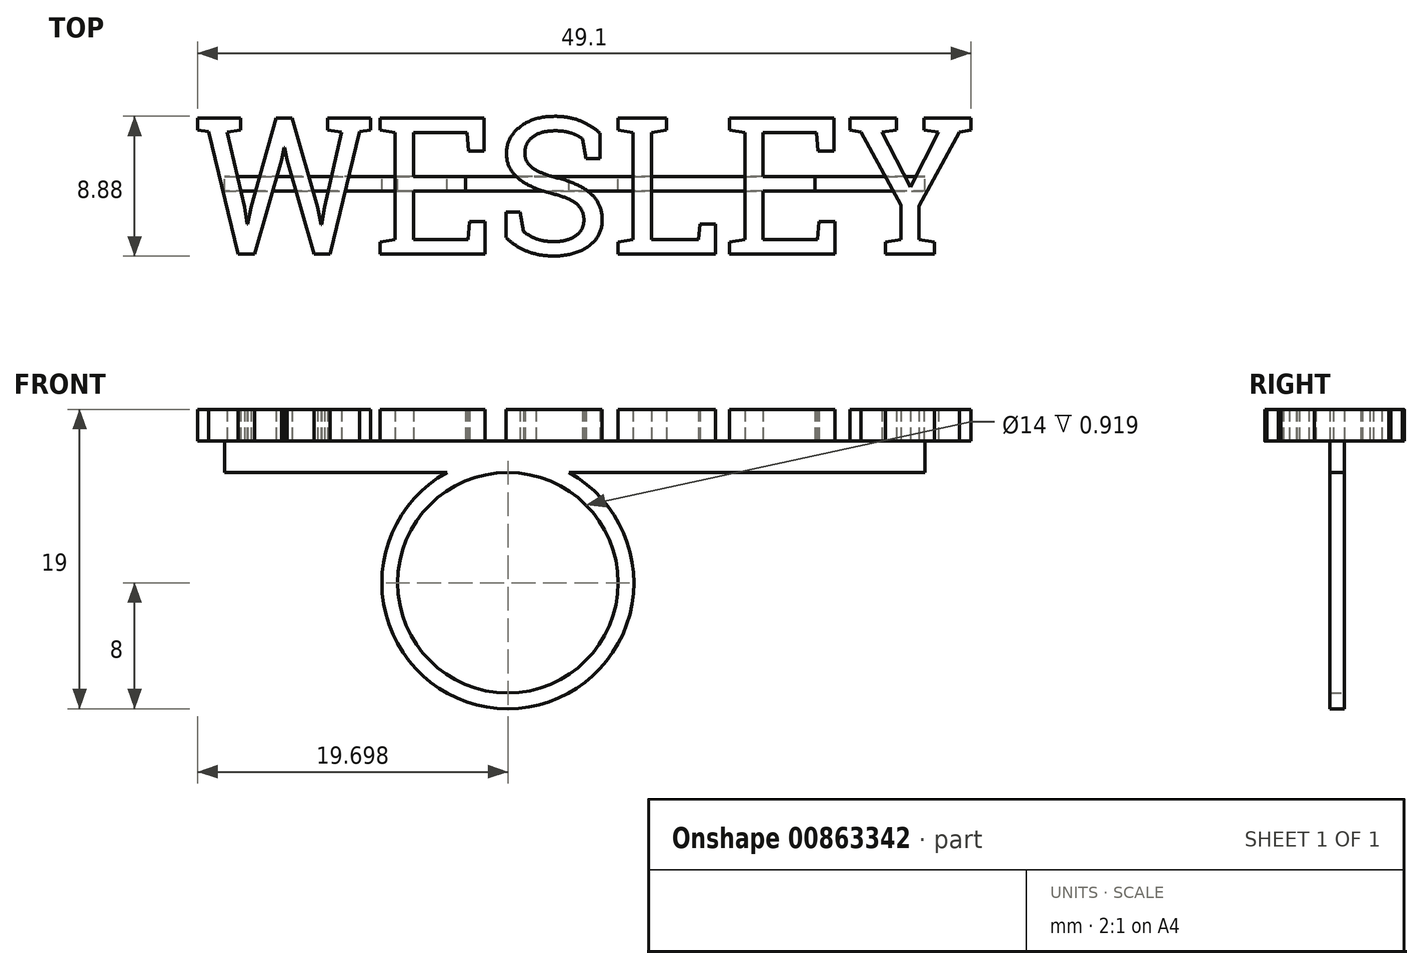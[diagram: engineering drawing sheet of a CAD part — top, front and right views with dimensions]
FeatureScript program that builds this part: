
annotation { "Feature Type Name" : "Feature", "Feature Type Description" : "" }
export const myFeature = defineFeature(function(context is Context, id is Id, definition is map)
    precondition{}
    {
        {
            var Q0;
            Q0=qCreatedBy(makeId("Top.planeOp"),FACE);
            var sketch = newSketch(context, id + "F0", { "sketchPlane" : qUnion([Q0])});
            skText(sketch, "E0", { "text": "WESLEY", "fontName": "RobotoSlab-Regular.ttf"});
            const initialGuessF0  = {"E0": [0, 0, 1, 0, 0.00873]};
            skSetInitialGuess(sketch, initialGuessF0);
            skSolve(sketch);
        }
        {
            var Q0;
            Q0=qSketchRegion(id+"F0",true);
            extrude(context, id + "F1", {"entities" : qUnion([Q0]), "depth" : 2 * mm, "offsetDistance" : 25 * mm});
        }
        {
            var Q0;
            Q0=makeQuery(id+"F1.opExtrude","CAP_FACE",FACE,{"disambiguationData":[OSD([sQuery(id+"F0.wireOp",EDGE,"E0.sketch_text.stroke-30"),sQuery(id+"F0.wireOp",EDGE,"E0.sketch_text.stroke-31"),sQuery(id+"F0.wireOp",EDGE,"E0.sketch_text.stroke-32"),sQuery(id+"F0.wireOp",EDGE,"E0.sketch_text.stroke-33"),sQuery(id+"F0.wireOp",EDGE,"E0.sketch_text.stroke-34"),sQuery(id+"F0.wireOp",EDGE,"E0.sketch_text.stroke-35"),sQuery(id+"F0.wireOp",EDGE,"E0.sketch_text.stroke-36"),sQuery(id+"F0.wireOp",EDGE,"E0.sketch_text.stroke-37"),sQuery(id+"F0.wireOp",EDGE,"E0.sketch_text.stroke-38"),sQuery(id+"F0.wireOp",EDGE,"E0.sketch_text.stroke-39"),sQuery(id+"F0.wireOp",EDGE,"E0.sketch_text.stroke-40"),sQuery(id+"F0.wireOp",EDGE,"E0.sketch_text.stroke-41"),sQuery(id+"F0.wireOp",EDGE,"E0.sketch_text.stroke-42"),sQuery(id+"F0.wireOp",EDGE,"E0.sketch_text.stroke-43"),sQuery(id+"F0.wireOp",EDGE,"E0.sketch_text.stroke-44"),sQuery(id+"F0.wireOp",EDGE,"E0.sketch_text.stroke-45"),sQuery(id+"F0.wireOp",EDGE,"E0.sketch_text.stroke-46"),sQuery(id+"F0.wireOp",EDGE,"E0.sketch_text.stroke-47"),sQuery(id+"F0.wireOp",EDGE,"E0.sketch_text.stroke-48"),sQuery(id+"F0.wireOp",EDGE,"E0.sketch_text.stroke-49")])],"isStart":true});
            var sketch = newSketch(context, id + "F2", { "sketchPlane" : qUnion([Q0])});
            skLineSegment(sketch, "E1.bottom", {"start": v(13.86, -4) * mm, "end": v(46.36, -4) * mm});
            skLineSegment(sketch, "E1.top", {"start": v(13.86, -4.91) * mm, "end": v(46.36, -4.91) * mm});
            skLineSegment(sketch, "E1.left", {"start": v(13.86, -4) * mm, "end": v(13.86, -4.91) * mm});
            skLineSegment(sketch, "E1.right", {"start": v(46.36, -4) * mm, "end": v(46.36, -4.91) * mm});
            skLineSegment(sketch, "E2.bottom", {"start": v(13.86, -4) * mm, "end": v(1.86, -4) * mm});
            skLineSegment(sketch, "E2.top", {"start": v(13.86, -4.91) * mm, "end": v(1.86, -4.91) * mm});
            skLineSegment(sketch, "E2.right", {"start": v(1.86, -4) * mm, "end": v(1.86, -4.91) * mm});
            skSolve(sketch);
        }
        {
            var Q0;
            Q0=qSketchRegion(id+"F2",true);
            extrude(context, id + "F3", {"entities" : qUnion([Q0]), "depth" : 2 * mm, "offsetDistance" : 25 * mm});
        }
        {
            var Q0;
            Q0=makeQuery(id+"F1.opExtrude","SWEPT_BODY",BODY,{"disambiguationData":[OSD([sQuery(id+"F0.wireOp",EDGE,"E0.sketch_text.stroke-0"),sQuery(id+"F0.wireOp",EDGE,"E0.sketch_text.stroke-1"),sQuery(id+"F0.wireOp",EDGE,"E0.sketch_text.stroke-2"),sQuery(id+"F0.wireOp",EDGE,"E0.sketch_text.stroke-3"),sQuery(id+"F0.wireOp",EDGE,"E0.sketch_text.stroke-4"),sQuery(id+"F0.wireOp",EDGE,"E0.sketch_text.stroke-5"),sQuery(id+"F0.wireOp",EDGE,"E0.sketch_text.stroke-6"),sQuery(id+"F0.wireOp",EDGE,"E0.sketch_text.stroke-7"),sQuery(id+"F0.wireOp",EDGE,"E0.sketch_text.stroke-8"),sQuery(id+"F0.wireOp",EDGE,"E0.sketch_text.stroke-9"),sQuery(id+"F0.wireOp",EDGE,"E0.sketch_text.stroke-10"),sQuery(id+"F0.wireOp",EDGE,"E0.sketch_text.stroke-11"),sQuery(id+"F0.wireOp",EDGE,"E0.sketch_text.stroke-12"),sQuery(id+"F0.wireOp",EDGE,"E0.sketch_text.stroke-13"),sQuery(id+"F0.wireOp",EDGE,"E0.sketch_text.stroke-14"),sQuery(id+"F0.wireOp",EDGE,"E0.sketch_text.stroke-15"),sQuery(id+"F0.wireOp",EDGE,"E0.sketch_text.stroke-16"),sQuery(id+"F0.wireOp",EDGE,"E0.sketch_text.stroke-17"),sQuery(id+"F0.wireOp",EDGE,"E0.sketch_text.stroke-18"),sQuery(id+"F0.wireOp",EDGE,"E0.sketch_text.stroke-19"),sQuery(id+"F0.wireOp",EDGE,"E0.sketch_text.stroke-20"),sQuery(id+"F0.wireOp",EDGE,"E0.sketch_text.stroke-21"),sQuery(id+"F0.wireOp",EDGE,"E0.sketch_text.stroke-22"),sQuery(id+"F0.wireOp",EDGE,"E0.sketch_text.stroke-23"),sQuery(id+"F0.wireOp",EDGE,"E0.sketch_text.stroke-24"),sQuery(id+"F0.wireOp",EDGE,"E0.sketch_text.stroke-25"),sQuery(id+"F0.wireOp",EDGE,"E0.sketch_text.stroke-26"),sQuery(id+"F0.wireOp",EDGE,"E0.sketch_text.stroke-27"),sQuery(id+"F0.wireOp",EDGE,"E0.sketch_text.stroke-28"),sQuery(id+"F0.wireOp",EDGE,"E0.sketch_text.stroke-29")])]});
            var Q1;
            Q1=makeQuery(id+"F3.opExtrude","SWEPT_BODY",BODY,{"disambiguationData":[OSD([sQuery(id+"F2.wireOp",EDGE,"E1.bottom"),sQuery(id+"F2.wireOp",EDGE,"E1.top"),sQuery(id+"F2.wireOp",EDGE,"E1.right"),sQuery(id+"F2.wireOp",EDGE,"E2.bottom"),sQuery(id+"F2.wireOp",EDGE,"E2.top"),sQuery(id+"F2.wireOp",EDGE,"E2.right")])]});
            var Q2;
            Q2=makeQuery(id+"F1.opExtrude","SWEPT_BODY",BODY,{"disambiguationData":[OSD([sQuery(id+"F0.wireOp",EDGE,"E0.sketch_text.stroke-30"),sQuery(id+"F0.wireOp",EDGE,"E0.sketch_text.stroke-31"),sQuery(id+"F0.wireOp",EDGE,"E0.sketch_text.stroke-32"),sQuery(id+"F0.wireOp",EDGE,"E0.sketch_text.stroke-33"),sQuery(id+"F0.wireOp",EDGE,"E0.sketch_text.stroke-34"),sQuery(id+"F0.wireOp",EDGE,"E0.sketch_text.stroke-35"),sQuery(id+"F0.wireOp",EDGE,"E0.sketch_text.stroke-36"),sQuery(id+"F0.wireOp",EDGE,"E0.sketch_text.stroke-37"),sQuery(id+"F0.wireOp",EDGE,"E0.sketch_text.stroke-38"),sQuery(id+"F0.wireOp",EDGE,"E0.sketch_text.stroke-39"),sQuery(id+"F0.wireOp",EDGE,"E0.sketch_text.stroke-40"),sQuery(id+"F0.wireOp",EDGE,"E0.sketch_text.stroke-41"),sQuery(id+"F0.wireOp",EDGE,"E0.sketch_text.stroke-42"),sQuery(id+"F0.wireOp",EDGE,"E0.sketch_text.stroke-43"),sQuery(id+"F0.wireOp",EDGE,"E0.sketch_text.stroke-44"),sQuery(id+"F0.wireOp",EDGE,"E0.sketch_text.stroke-45"),sQuery(id+"F0.wireOp",EDGE,"E0.sketch_text.stroke-46"),sQuery(id+"F0.wireOp",EDGE,"E0.sketch_text.stroke-47"),sQuery(id+"F0.wireOp",EDGE,"E0.sketch_text.stroke-48"),sQuery(id+"F0.wireOp",EDGE,"E0.sketch_text.stroke-49")])]});
            var Q3;
            Q3=makeQuery(id+"F1.opExtrude","SWEPT_BODY",BODY,{"disambiguationData":[OSD([sQuery(id+"F0.wireOp",EDGE,"E0.sketch_text.stroke-50"),sQuery(id+"F0.wireOp",EDGE,"E0.sketch_text.stroke-51"),sQuery(id+"F0.wireOp",EDGE,"E0.sketch_text.stroke-52"),sQuery(id+"F0.wireOp",EDGE,"E0.sketch_text.stroke-53"),sQuery(id+"F0.wireOp",EDGE,"E0.sketch_text.stroke-54"),sQuery(id+"F0.wireOp",EDGE,"E0.sketch_text.stroke-55"),sQuery(id+"F0.wireOp",EDGE,"E0.sketch_text.stroke-56"),sQuery(id+"F0.wireOp",EDGE,"E0.sketch_text.stroke-57"),sQuery(id+"F0.wireOp",EDGE,"E0.sketch_text.stroke-58"),sQuery(id+"F0.wireOp",EDGE,"E0.sketch_text.stroke-59"),sQuery(id+"F0.wireOp",EDGE,"E0.sketch_text.stroke-60"),sQuery(id+"F0.wireOp",EDGE,"E0.sketch_text.stroke-61"),sQuery(id+"F0.wireOp",EDGE,"E0.sketch_text.stroke-62"),sQuery(id+"F0.wireOp",EDGE,"E0.sketch_text.stroke-63"),sQuery(id+"F0.wireOp",EDGE,"E0.sketch_text.stroke-64"),sQuery(id+"F0.wireOp",EDGE,"E0.sketch_text.stroke-65"),sQuery(id+"F0.wireOp",EDGE,"E0.sketch_text.stroke-66"),sQuery(id+"F0.wireOp",EDGE,"E0.sketch_text.stroke-67"),sQuery(id+"F0.wireOp",EDGE,"E0.sketch_text.stroke-68"),sQuery(id+"F0.wireOp",EDGE,"E0.sketch_text.stroke-69"),sQuery(id+"F0.wireOp",EDGE,"E0.sketch_text.stroke-70"),sQuery(id+"F0.wireOp",EDGE,"E0.sketch_text.stroke-71"),sQuery(id+"F0.wireOp",EDGE,"E0.sketch_text.stroke-72"),sQuery(id+"F0.wireOp",EDGE,"E0.sketch_text.stroke-73"),sQuery(id+"F0.wireOp",EDGE,"E0.sketch_text.stroke-74"),sQuery(id+"F0.wireOp",EDGE,"E0.sketch_text.stroke-75"),sQuery(id+"F0.wireOp",EDGE,"E0.sketch_text.stroke-76"),sQuery(id+"F0.wireOp",EDGE,"E0.sketch_text.stroke-77"),sQuery(id+"F0.wireOp",EDGE,"E0.sketch_text.stroke-78"),sQuery(id+"F0.wireOp",EDGE,"E0.sketch_text.stroke-79")])]});
            var Q4;
            Q4=makeQuery(id+"F1.opExtrude","SWEPT_BODY",BODY,{"disambiguationData":[OSD([sQuery(id+"F0.wireOp",EDGE,"E0.sketch_text.stroke-80"),sQuery(id+"F0.wireOp",EDGE,"E0.sketch_text.stroke-81"),sQuery(id+"F0.wireOp",EDGE,"E0.sketch_text.stroke-82"),sQuery(id+"F0.wireOp",EDGE,"E0.sketch_text.stroke-83"),sQuery(id+"F0.wireOp",EDGE,"E0.sketch_text.stroke-84"),sQuery(id+"F0.wireOp",EDGE,"E0.sketch_text.stroke-85"),sQuery(id+"F0.wireOp",EDGE,"E0.sketch_text.stroke-86"),sQuery(id+"F0.wireOp",EDGE,"E0.sketch_text.stroke-87"),sQuery(id+"F0.wireOp",EDGE,"E0.sketch_text.stroke-88"),sQuery(id+"F0.wireOp",EDGE,"E0.sketch_text.stroke-89"),sQuery(id+"F0.wireOp",EDGE,"E0.sketch_text.stroke-90"),sQuery(id+"F0.wireOp",EDGE,"E0.sketch_text.stroke-91"),sQuery(id+"F0.wireOp",EDGE,"E0.sketch_text.stroke-92"),sQuery(id+"F0.wireOp",EDGE,"E0.sketch_text.stroke-93"),sQuery(id+"F0.wireOp",EDGE,"E0.sketch_text.stroke-94"),sQuery(id+"F0.wireOp",EDGE,"E0.sketch_text.stroke-95")])]});
            var Q5;
            Q5=makeQuery(id+"F1.opExtrude","SWEPT_BODY",BODY,{"disambiguationData":[OSD([sQuery(id+"F0.wireOp",EDGE,"E0.sketch_text.stroke-96"),sQuery(id+"F0.wireOp",EDGE,"E0.sketch_text.stroke-97"),sQuery(id+"F0.wireOp",EDGE,"E0.sketch_text.stroke-98"),sQuery(id+"F0.wireOp",EDGE,"E0.sketch_text.stroke-99"),sQuery(id+"F0.wireOp",EDGE,"E0.sketch_text.stroke-100"),sQuery(id+"F0.wireOp",EDGE,"E0.sketch_text.stroke-101"),sQuery(id+"F0.wireOp",EDGE,"E0.sketch_text.stroke-102"),sQuery(id+"F0.wireOp",EDGE,"E0.sketch_text.stroke-103"),sQuery(id+"F0.wireOp",EDGE,"E0.sketch_text.stroke-104"),sQuery(id+"F0.wireOp",EDGE,"E0.sketch_text.stroke-105"),sQuery(id+"F0.wireOp",EDGE,"E0.sketch_text.stroke-106"),sQuery(id+"F0.wireOp",EDGE,"E0.sketch_text.stroke-107"),sQuery(id+"F0.wireOp",EDGE,"E0.sketch_text.stroke-108"),sQuery(id+"F0.wireOp",EDGE,"E0.sketch_text.stroke-109"),sQuery(id+"F0.wireOp",EDGE,"E0.sketch_text.stroke-110"),sQuery(id+"F0.wireOp",EDGE,"E0.sketch_text.stroke-111"),sQuery(id+"F0.wireOp",EDGE,"E0.sketch_text.stroke-112"),sQuery(id+"F0.wireOp",EDGE,"E0.sketch_text.stroke-113"),sQuery(id+"F0.wireOp",EDGE,"E0.sketch_text.stroke-114"),sQuery(id+"F0.wireOp",EDGE,"E0.sketch_text.stroke-115")])]});
            var Q6;
            Q6=makeQuery(id+"F1.opExtrude","SWEPT_BODY",BODY,{"disambiguationData":[OSD([sQuery(id+"F0.wireOp",EDGE,"E0.sketch_text.stroke-116"),sQuery(id+"F0.wireOp",EDGE,"E0.sketch_text.stroke-117"),sQuery(id+"F0.wireOp",EDGE,"E0.sketch_text.stroke-118"),sQuery(id+"F0.wireOp",EDGE,"E0.sketch_text.stroke-119"),sQuery(id+"F0.wireOp",EDGE,"E0.sketch_text.stroke-120"),sQuery(id+"F0.wireOp",EDGE,"E0.sketch_text.stroke-121"),sQuery(id+"F0.wireOp",EDGE,"E0.sketch_text.stroke-122"),sQuery(id+"F0.wireOp",EDGE,"E0.sketch_text.stroke-123"),sQuery(id+"F0.wireOp",EDGE,"E0.sketch_text.stroke-124"),sQuery(id+"F0.wireOp",EDGE,"E0.sketch_text.stroke-125"),sQuery(id+"F0.wireOp",EDGE,"E0.sketch_text.stroke-126"),sQuery(id+"F0.wireOp",EDGE,"E0.sketch_text.stroke-127"),sQuery(id+"F0.wireOp",EDGE,"E0.sketch_text.stroke-128"),sQuery(id+"F0.wireOp",EDGE,"E0.sketch_text.stroke-129"),sQuery(id+"F0.wireOp",EDGE,"E0.sketch_text.stroke-130"),sQuery(id+"F0.wireOp",EDGE,"E0.sketch_text.stroke-131"),sQuery(id+"F0.wireOp",EDGE,"E0.sketch_text.stroke-132"),sQuery(id+"F0.wireOp",EDGE,"E0.sketch_text.stroke-133"),sQuery(id+"F0.wireOp",EDGE,"E0.sketch_text.stroke-134"),sQuery(id+"F0.wireOp",EDGE,"E0.sketch_text.stroke-135"),sQuery(id+"F0.wireOp",EDGE,"E0.sketch_text.stroke-136")])]});
            booleanBodies(context, id + "F4", {"operationType" : BooleanOperationType.UNION, "tools" : qUnion([Q0, Q1, Q2, Q3, Q4, Q5, Q6])});
        }
        {
            var Q0;
            Q0=makeQuery(id+"F4.opBoolean","MERGE",FACE,{"derivedFrom":[makeQuery(id+"F1.opExtrude","SWEPT_FACE",FACE,{"disambiguationData":[OSD([sQuery(id+"F0.wireOp",EDGE,"E0.sketch_text.stroke-41")])]}),makeQuery(id+"F1.opExtrude","SWEPT_FACE",FACE,{"disambiguationData":[OSD([sQuery(id+"F0.wireOp",EDGE,"E0.sketch_text.stroke-107")])]}),makeQuery(id+"F3.opExtrude","SWEPT_FACE",FACE,{"disambiguationData":[OSD([sQuery(id+"F2.wireOp",EDGE,"E1.top"),sQuery(id+"F2.wireOp",EDGE,"E2.top")])]})]});
            var sketch = newSketch(context, id + "F5", { "sketchPlane" : qUnion([Q0])});
            skCircle(sketch, "E3", {"center": v(-19.86, -9) * mm, "radius": 7 * mm});
            skLineSegment(sketch, "E4", {"start": v(-1.86, -2) * mm, "end": v(-19.86, -2) * mm, "construction": true});
            skCircle(sketch, "E5", {"center": v(-19.86, -9) * mm, "radius": 8 * mm});
            skSolve(sketch);
        }
        {
            var Q0;
            {var subQ0=sQuery(id+"F5.wireOp",EDGE,"E3");Q0=makeQuery(id+"F5.imprint","IMPRINT",FACE,{"disambiguationData":[TD([[makeQuery(id+"F5.imprint","IMPRINT",EDGE,{"derivedFrom":subQ0}),-1.0]])]});}
            var Q1;
            {var subQ0=sQuery(id+"F5.wireOp",EDGE,"E5");var subQ1=makeQuery(id+"F3.opExtrude","CAP_EDGE",EDGE,{"disambiguationData":[OSD([sQuery(id+"F2.wireOp",EDGE,"E1.top"),sQuery(id+"F2.wireOp",EDGE,"E2.top")])],"isStart":false});var subQ2=makeQuery(id+"F5.imprint","INTERSECT",VERTEX,{"disambiguationData":[OD(0.0)],"derivedFrom":[subQ1,subQ0]});Q1=makeQuery(id+"F5.imprint","IMPRINT",FACE,{"disambiguationData":[TD([[makeQuery(id+"F5.imprint","IMPRINT",EDGE,{"disambiguationData":[TD([[subQ2,1.0]])],"derivedFrom":subQ0}),1.0]])]});}
            var Q2;
            Q2=makeQuery(id+"F4.opBoolean","MERGE",FACE,{"derivedFrom":[makeQuery(id+"F1.opExtrude","SWEPT_FACE",FACE,{"disambiguationData":[OSD([sQuery(id+"F0.wireOp",EDGE,"E0.sketch_text.stroke-43")])]}),makeQuery(id+"F1.opExtrude","SWEPT_FACE",FACE,{"disambiguationData":[OSD([sQuery(id+"F0.wireOp",EDGE,"E0.sketch_text.stroke-109")])]}),makeQuery(id+"F3.opExtrude","SWEPT_FACE",FACE,{"disambiguationData":[OSD([sQuery(id+"F2.wireOp",EDGE,"E1.bottom"),sQuery(id+"F2.wireOp",EDGE,"E2.bottom")])]})]});
            extrude(context, id + "F6", {"entities" : qUnion([Q0, Q1]), "operationType" : NewBodyOperationType.ADD, "endBound" : BoundingType.UP_TO_SURFACE, "oppositeDirection" : true, "depth" : 25 * mm, "endBoundEntityFace" : qUnion([Q2]), "offsetDistance" : 25 * mm});
        }
    });
